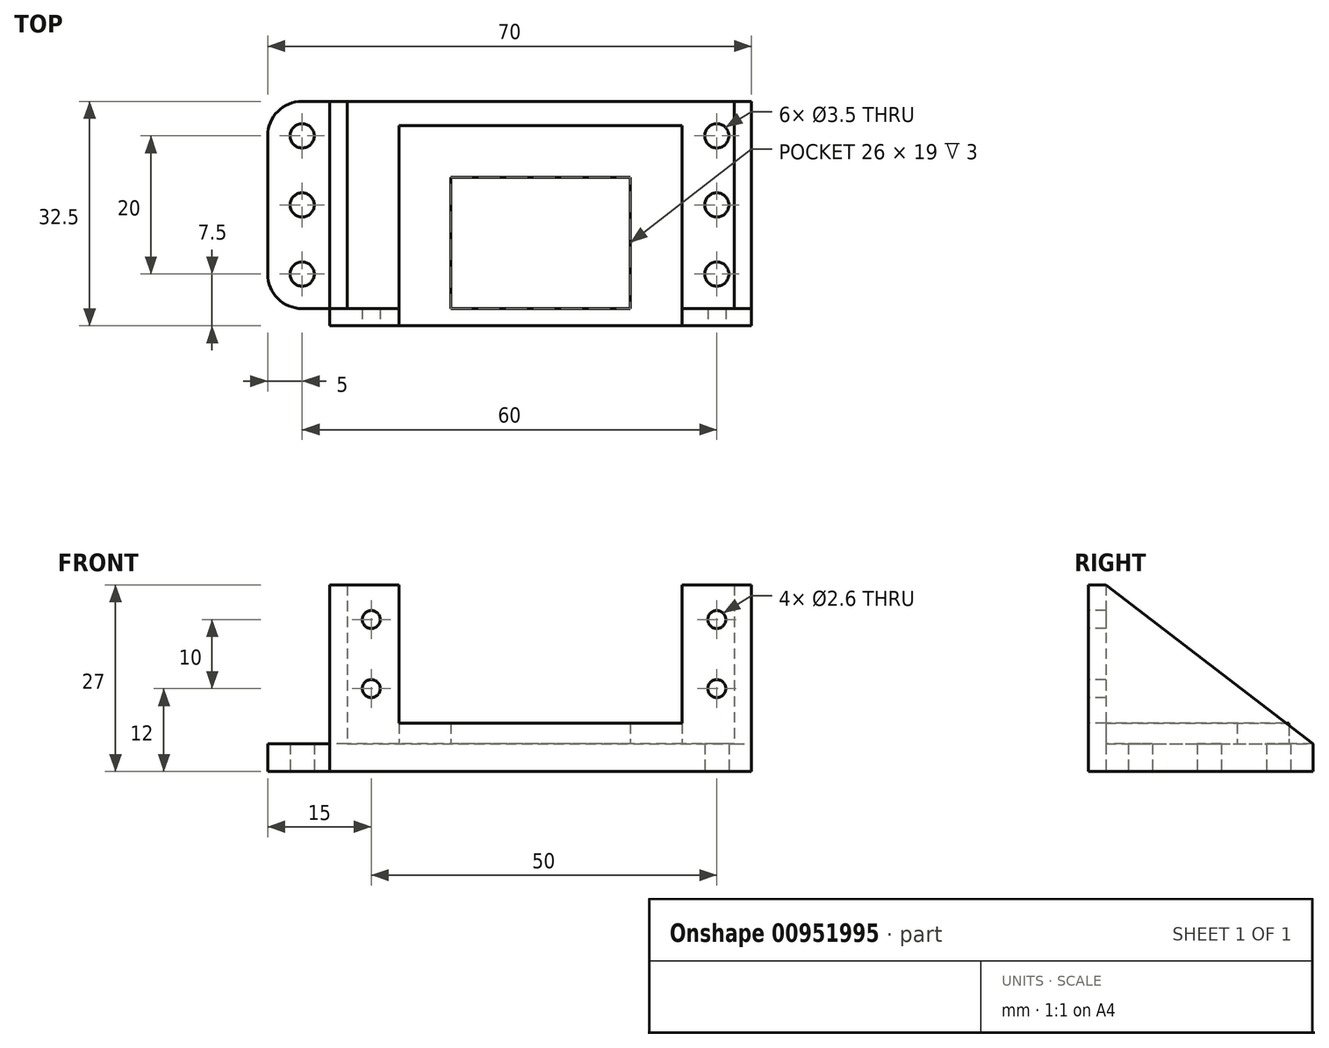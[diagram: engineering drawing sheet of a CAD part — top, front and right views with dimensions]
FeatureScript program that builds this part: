
annotation { "Feature Type Name" : "Feature", "Feature Type Description" : "" }
export const myFeature = defineFeature(function(context is Context, id is Id, definition is map)
    precondition{}
    {
        {
            var Q0;
            Q0=qCreatedBy(makeId("Top.planeOp"),FACE);
            var sketch = newSketch(context, id + "F0", { "sketchPlane" : qUnion([Q0])});
            skPoint(sketch, "E0", {"position": v(0, 0) * mm});
            skPoint(sketch, "E1.0.1.0", {"position": v(0, 10) * mm});
            skPoint(sketch, "E1.0.2.0", {"position": v(0, 20) * mm});
            skPoint(sketch, "E1.0.3.0", {"position": v(0, 30) * mm});
            skPoint(sketch, "E1.0.4.0", {"position": v(0, 40) * mm});
            skPoint(sketch, "E1.0.5.0", {"position": v(0, 50) * mm});
            skPoint(sketch, "E1.0.6.0", {"position": v(0, 60) * mm});
            skPoint(sketch, "E1.1.0.0", {"position": v(10, 0) * mm});
            skPoint(sketch, "E1.1.1.0", {"position": v(10, 10) * mm});
            skPoint(sketch, "E1.1.2.0", {"position": v(10, 20) * mm});
            skPoint(sketch, "E1.1.3.0", {"position": v(10, 30) * mm});
            skPoint(sketch, "E1.1.4.0", {"position": v(10, 40) * mm});
            skPoint(sketch, "E1.1.5.0", {"position": v(10, 50) * mm});
            skPoint(sketch, "E1.1.6.0", {"position": v(10, 60) * mm});
            skPoint(sketch, "E1.2.0.0", {"position": v(20, 0) * mm});
            skPoint(sketch, "E1.2.1.0", {"position": v(20, 10) * mm});
            skPoint(sketch, "E1.2.2.0", {"position": v(20, 20) * mm});
            skPoint(sketch, "E1.2.3.0", {"position": v(20, 30) * mm});
            skPoint(sketch, "E1.2.4.0", {"position": v(20, 40) * mm});
            skPoint(sketch, "E1.2.5.0", {"position": v(20, 50) * mm});
            skPoint(sketch, "E1.2.6.0", {"position": v(20, 60) * mm});
            skPoint(sketch, "E1.3.0.0", {"position": v(30, 0) * mm});
            skPoint(sketch, "E1.3.1.0", {"position": v(30, 10) * mm});
            skPoint(sketch, "E1.3.2.0", {"position": v(30, 20) * mm});
            skPoint(sketch, "E1.3.3.0", {"position": v(30, 30) * mm});
            skPoint(sketch, "E1.3.4.0", {"position": v(30, 40) * mm});
            skPoint(sketch, "E1.3.5.0", {"position": v(30, 50) * mm});
            skPoint(sketch, "E1.3.6.0", {"position": v(30, 60) * mm});
            skPoint(sketch, "E1.4.0.0", {"position": v(40, 0) * mm});
            skPoint(sketch, "E1.4.1.0", {"position": v(40, 10) * mm});
            skPoint(sketch, "E1.4.2.0", {"position": v(40, 20) * mm});
            skPoint(sketch, "E1.5.0.0", {"position": v(50, 0) * mm});
            skPoint(sketch, "E1.5.1.0", {"position": v(50, 10) * mm});
            skPoint(sketch, "E1.5.2.0", {"position": v(50, 20) * mm});
            skPoint(sketch, "E1.6.0.0", {"position": v(60, 0) * mm});
            skPoint(sketch, "E1.6.1.0", {"position": v(60, 10) * mm});
            skPoint(sketch, "E1.6.2.0", {"position": v(60, 20) * mm});
            skPoint(sketch, "E1.7.0.0", {"position": v(70, 0) * mm});
            skPoint(sketch, "E1.7.1.0", {"position": v(70, 10) * mm});
            skPoint(sketch, "E1.7.2.0", {"position": v(70, 20) * mm});
            skPoint(sketch, "E1.8.0.0", {"position": v(80, 0) * mm});
            skPoint(sketch, "E1.8.1.0", {"position": v(80, 10) * mm});
            skPoint(sketch, "E1.8.2.0", {"position": v(80, 20) * mm});
            skPoint(sketch, "E1.8.3.0", {"position": v(80, 30) * mm});
            skPoint(sketch, "E1.8.4.0", {"position": v(80, 40) * mm});
            skPoint(sketch, "E1.8.5.0", {"position": v(80, 50) * mm});
            skPoint(sketch, "E1.8.6.0", {"position": v(80, 60) * mm});
            skPoint(sketch, "E1.9.0.0", {"position": v(90, 0) * mm});
            skPoint(sketch, "E1.9.1.0", {"position": v(90, 10) * mm});
            skPoint(sketch, "E1.9.2.0", {"position": v(90, 20) * mm});
            skPoint(sketch, "E1.9.3.0", {"position": v(90, 30) * mm});
            skPoint(sketch, "E1.9.4.0", {"position": v(90, 40) * mm});
            skPoint(sketch, "E1.9.5.0", {"position": v(90, 50) * mm});
            skPoint(sketch, "E1.9.6.0", {"position": v(90, 60) * mm});
            skLineSegment(sketch, "E1.direction1", {"start": v(0, 0) * mm, "end": v(10, 0) * mm, "construction": true});
            skLineSegment(sketch, "E1.direction2", {"start": v(0, 0) * mm, "end": v(0, 10) * mm, "construction": true});
            skPoint(sketch, "E2.0.10.0", {"position": v(100, 0) * mm});
            skPoint(sketch, "E2.0.10.1", {"position": v(100, 10) * mm});
            skPoint(sketch, "E2.0.10.2", {"position": v(100, 20) * mm});
            skPoint(sketch, "E2.0.10.3", {"position": v(100, 30) * mm});
            skPoint(sketch, "E2.0.10.4", {"position": v(100, 40) * mm});
            skPoint(sketch, "E2.0.10.5", {"position": v(100, 50) * mm});
            skPoint(sketch, "E2.0.10.6", {"position": v(100, 60) * mm});
            skPoint(sketch, "E3.0.0.7", {"position": v(0, 70) * mm});
            skPoint(sketch, "E3.0.1.7", {"position": v(10, 70) * mm});
            skPoint(sketch, "E3.0.2.7", {"position": v(20, 70) * mm});
            skPoint(sketch, "E3.0.3.7", {"position": v(30, 70) * mm});
            skPoint(sketch, "E3.0.4.7", {"position": v(40, 70) * mm});
            skPoint(sketch, "E3.0.5.7", {"position": v(50, 70) * mm});
            skPoint(sketch, "E3.0.6.7", {"position": v(60, 70) * mm});
            skPoint(sketch, "E3.0.7.7", {"position": v(70, 70) * mm});
            skPoint(sketch, "E3.0.8.7", {"position": v(80, 70) * mm});
            skPoint(sketch, "E3.0.9.7", {"position": v(90, 70) * mm});
            skPoint(sketch, "E3.0.10.7", {"position": v(100, 70) * mm});
            skPoint(sketch, "E4.0.11.0", {"position": v(110, 0) * mm});
            skPoint(sketch, "E4.0.11.1", {"position": v(110, 10) * mm});
            skPoint(sketch, "E4.0.11.2", {"position": v(110, 20) * mm});
            skPoint(sketch, "E4.0.11.3", {"position": v(110, 30) * mm});
            skPoint(sketch, "E4.0.11.4", {"position": v(110, 40) * mm});
            skPoint(sketch, "E4.0.11.5", {"position": v(110, 50) * mm});
            skPoint(sketch, "E4.0.11.6", {"position": v(110, 60) * mm});
            skPoint(sketch, "E4.0.11.7", {"position": v(110, 70) * mm});
            skLineSegment(sketch, "E5", {"start": v(5, 24) * mm, "end": v(5, 11) * mm});
            skLineSegment(sketch, "E6", {"start": v(6, 10) * mm, "end": v(104, 10) * mm});
            skLineSegment(sketch, "E7", {"start": v(105, 11) * mm, "end": v(105, 24) * mm});
            skLineSegment(sketch, "E8", {"start": v(104, 25) * mm, "end": v(6, 25) * mm});
            skPoint(sketch, "E9.visualSharp", {"position": v(5, 25) * mm});
            skArc(sketch, "E9.filletArc", {"start": v(6, 25) * mm, "mid": v(5.3, 24.7) * mm, "end": v(5, 24) * mm});
            skPoint(sketch, "E10.visualSharp", {"position": v(5, 10) * mm});
            skArc(sketch, "E10.filletArc", {"start": v(5, 11) * mm, "mid": v(5.3, 10.3) * mm, "end": v(6, 10) * mm});
            skPoint(sketch, "E11.visualSharp", {"position": v(105, 25) * mm});
            skArc(sketch, "E11.filletArc", {"start": v(105, 24) * mm, "mid": v(104.7, 24.7) * mm, "end": v(104, 25) * mm});
            skPoint(sketch, "E12.visualSharp", {"position": v(105, 10) * mm});
            skArc(sketch, "E12.filletArc", {"start": v(104, 10) * mm, "mid": v(104.7, 10.3) * mm, "end": v(105, 11) * mm});
            skLineSegment(sketch, "E13", {"start": v(55, 10) * mm, "end": v(55, 76.51) * mm});
            skSolve(sketch);
        }
        {
            var Q0;
            Q0=qCreatedBy(makeId("Top.planeOp"),FACE);
            var sketch = newSketch(context, id + "F1", { "sketchPlane" : qUnion([Q0])});
            skLineSegment(sketch, "E14.0", {"start": v(104, 25) * mm, "end": v(6, 25) * mm});
            skLineSegment(sketch, "E15.bottom", {"start": v(36.5, 35) * mm, "end": v(92.5, 35) * mm});
            skLineSegment(sketch, "E15.top", {"start": v(36.5, 32.5) * mm, "end": v(92.5, 32.5) * mm});
            skLineSegment(sketch, "E15.left", {"start": v(36.5, 35) * mm, "end": v(36.5, 32.5) * mm});
            skLineSegment(sketch, "E15.right", {"start": v(92.5, 35) * mm, "end": v(92.5, 32.5) * mm});
            skLineSegment(sketch, "E16", {"start": v(44, 35) * mm, "end": v(44, 32.5) * mm});
            skLineSegment(sketch, "E17", {"start": v(85, 35) * mm, "end": v(85, 32.5) * mm});
            skLineSegment(sketch, "E18", {"start": v(36.5, 35) * mm, "end": v(25, 35) * mm});
            skLineSegment(sketch, "E19", {"start": v(25, 35) * mm, "end": v(25, 65) * mm});
            skLineSegment(sketch, "E20", {"start": v(25, 65) * mm, "end": v(36.5, 65) * mm});
            skLineSegment(sketch, "E21", {"start": v(36.5, 65) * mm, "end": v(95, 65) * mm});
            skLineSegment(sketch, "E22", {"start": v(95, 65) * mm, "end": v(95, 35) * mm});
            skLineSegment(sketch, "E23", {"start": v(95, 35) * mm, "end": v(92.5, 35) * mm});
            skLineSegment(sketch, "E24", {"start": v(36.5, 32.5) * mm, "end": v(34, 32.5) * mm});
            skLineSegment(sketch, "E25", {"start": v(34, 32.5) * mm, "end": v(34, 35) * mm});
            skLineSegment(sketch, "E26", {"start": v(92.5, 32.5) * mm, "end": v(95, 32.5) * mm});
            skLineSegment(sketch, "E27", {"start": v(95, 32.5) * mm, "end": v(95, 35) * mm});
            skLineSegment(sketch, "E28", {"start": v(44, 35) * mm, "end": v(44, 61.5) * mm});
            skLineSegment(sketch, "E29", {"start": v(44, 61.5) * mm, "end": v(85, 61.5) * mm});
            skLineSegment(sketch, "E30", {"start": v(85, 61.5) * mm, "end": v(85, 35) * mm});
            skLineSegment(sketch, "E31", {"start": v(51.5, 35) * mm, "end": v(51.5, 54) * mm});
            skLineSegment(sketch, "E32", {"start": v(51.5, 54) * mm, "end": v(77.5, 54) * mm});
            skLineSegment(sketch, "E33", {"start": v(77.5, 54) * mm, "end": v(77.5, 35) * mm});
            skCircle(sketch, "E34", {"center": v(30, 40) * mm, "radius": 1.75 * mm});
            skCircle(sketch, "E35", {"center": v(30, 50) * mm, "radius": 1.75 * mm});
            skCircle(sketch, "E36", {"center": v(30, 60) * mm, "radius": 1.75 * mm});
            skCircle(sketch, "E37", {"center": v(90, 40) * mm, "radius": 1.75 * mm});
            skCircle(sketch, "E38", {"center": v(90, 50) * mm, "radius": 1.75 * mm});
            skCircle(sketch, "E39", {"center": v(90, 60) * mm, "radius": 1.75 * mm});
            skSolve(sketch);
        }
        {
            var Q0;
            {var subQ1=sQuery(id+"F1.wireOp",EDGE,"E19");Q0=makeQuery(id+"F1.imprint","IMPRINT",FACE,{"disambiguationData":[TD([[makeQuery(id+"F1.imprint","IMPRINT",EDGE,{"derivedFrom":subQ1}),-1.0]])]});}
            var Q1;
            {var subQ0=sQuery(id+"F1.wireOp",EDGE,"E28");Q1=makeQuery(id+"F1.imprint","IMPRINT",FACE,{"disambiguationData":[TD([[makeQuery(id+"F1.imprint","IMPRINT",EDGE,{"derivedFrom":subQ0}),-1.0]])]});}
            var Q2;
            {var subQ0=sQuery(id+"F1.wireOp",EDGE,"E31");Q2=makeQuery(id+"F1.imprint","IMPRINT",FACE,{"disambiguationData":[TD([[makeQuery(id+"F1.imprint","IMPRINT",EDGE,{"derivedFrom":subQ0}),-1.0]])]});}
            var Q3;
            {var subQ0=sQuery(id+"F1.wireOp",EDGE,"E15.left");Q3=makeQuery(id+"F1.imprint","IMPRINT",FACE,{"disambiguationData":[TD([[makeQuery(id+"F1.imprint","IMPRINT",EDGE,{"derivedFrom":subQ0}),-1.0]])]});}
            var Q4;
            {var subQ0=sQuery(id+"F1.wireOp",EDGE,"E15.left");Q4=makeQuery(id+"F1.imprint","IMPRINT",FACE,{"disambiguationData":[TD([[makeQuery(id+"F1.imprint","IMPRINT",EDGE,{"derivedFrom":subQ0}),1.0]])]});}
            var Q5;
            {var subQ4=sQuery(id+"F1.wireOp",EDGE,"E16");Q5=makeQuery(id+"F1.imprint","IMPRINT",FACE,{"disambiguationData":[TD([[makeQuery(id+"F1.imprint","IMPRINT",EDGE,{"derivedFrom":subQ4}),1.0]])]});}
            var Q6;
            {var subQ0=sQuery(id+"F1.wireOp",EDGE,"E15.right");Q6=makeQuery(id+"F1.imprint","IMPRINT",FACE,{"disambiguationData":[TD([[makeQuery(id+"F1.imprint","IMPRINT",EDGE,{"derivedFrom":subQ0}),-1.0]])]});}
            var Q7;
            Q7=makeQuery(id+"F1.imprint","IMPRINT",FACE,{"disambiguationData":[TD([[makeQuery(id+"F1.imprint","IMPRINT",EDGE,{"derivedFrom":sQuery(id+"F1.wireOp",EDGE,"E15.right")}),1.0]])]});
            extrude(context, id + "F2", {"entities" : qUnion([Q0, Q1, Q2, Q3, Q4, Q5, Q6, Q7]), "depth" : 4 * mm, "offsetDistance" : 25 * mm});
        }
        {
            var Q0;
            {var subQ0=sQuery(id+"F1.wireOp",EDGE,"E28");Q0=makeQuery(id+"F1.imprint","IMPRINT",FACE,{"disambiguationData":[TD([[makeQuery(id+"F1.imprint","IMPRINT",EDGE,{"derivedFrom":subQ0}),-1.0]])]});}
            var Q1;
            {var subQ4=sQuery(id+"F1.wireOp",EDGE,"E16");Q1=makeQuery(id+"F1.imprint","IMPRINT",FACE,{"disambiguationData":[TD([[makeQuery(id+"F1.imprint","IMPRINT",EDGE,{"derivedFrom":subQ4}),1.0]])]});}
            extrude(context, id + "F3", {"entities" : qUnion([Q0, Q1]), "operationType" : NewBodyOperationType.ADD, "depth" : (4 + 3) * mm, "offsetDistance" : 25 * mm});
        }
        {
            var Q0;
            {var subQ0=sQuery(id+"F1.wireOp",EDGE,"E15.left");Q0=makeQuery(id+"F1.imprint","IMPRINT",FACE,{"disambiguationData":[TD([[makeQuery(id+"F1.imprint","IMPRINT",EDGE,{"derivedFrom":subQ0}),1.0]])]});}
            var Q1;
            {var subQ0=sQuery(id+"F1.wireOp",EDGE,"E15.right");Q1=makeQuery(id+"F1.imprint","IMPRINT",FACE,{"disambiguationData":[TD([[makeQuery(id+"F1.imprint","IMPRINT",EDGE,{"derivedFrom":subQ0}),-1.0]])]});}
            var Q2;
            Q2=makeQuery(id+"F1.imprint","IMPRINT",FACE,{"disambiguationData":[TD([[makeQuery(id+"F1.imprint","IMPRINT",EDGE,{"derivedFrom":sQuery(id+"F1.wireOp",EDGE,"E15.right")}),1.0]])]});
            var Q3;
            {var subQ0=sQuery(id+"F1.wireOp",EDGE,"E15.left");Q3=makeQuery(id+"F1.imprint","IMPRINT",FACE,{"disambiguationData":[TD([[makeQuery(id+"F1.imprint","IMPRINT",EDGE,{"derivedFrom":subQ0}),-1.0]])]});}
            extrude(context, id + "F4", {"entities" : qUnion([Q0, Q1, Q2, Q3]), "operationType" : NewBodyOperationType.ADD, "depth" : 27 * mm, "offsetDistance" : 25 * mm});
        }
        {
            var Q0;
            {var subQ0=sQuery(id+"F1.wireOp",EDGE,"E27");Q0=makeQuery(id+"F4.boolean.opBoolean","MERGE",FACE,{"derivedFrom":[makeQuery(id+"F2.opExtrude","SWEPT_FACE",FACE,{"disambiguationData":[OSD([sQuery(id+"F1.wireOp",EDGE,"E22"),subQ0])]}),makeQuery(id+"F4.opExtrude","SWEPT_FACE",FACE,{"disambiguationData":[OSD([subQ0])]})]});}
            var sketch = newSketch(context, id + "F5", { "sketchPlane" : qUnion([Q0])});
            skLineSegment(sketch, "E40", {"start": v(35, 27) * mm, "end": v(65, 4) * mm});
            skSolve(sketch);
        }
        {
            var Q0;
            Q0=makeQuery(id+"F5.imprint","IMPRINT",FACE,{"disambiguationData":[TD([[makeQuery(id+"F5.imprint","IMPRINT",EDGE,{"derivedFrom":sQuery(id+"F5.wireOp",EDGE,"E40")}),-1.0]])]});
            extrude(context, id + "F6", {"entities" : qUnion([Q0]), "operationType" : NewBodyOperationType.ADD, "oppositeDirection" : true, "depth" : 2.5 * mm, "offsetDistance" : 25 * mm});
        }
        {
            var Q0;
            {var subQ0=sQuery(id+"F1.wireOp",EDGE,"E25");Q0=makeQuery(id+"F4.boolean.opBoolean","MERGE",FACE,{"derivedFrom":[makeQuery(id+"F2.opExtrude","SWEPT_FACE",FACE,{"disambiguationData":[OSD([subQ0])]}),makeQuery(id+"F4.opExtrude","SWEPT_FACE",FACE,{"disambiguationData":[OSD([subQ0])]})]});}
            var sketch = newSketch(context, id + "F7", { "sketchPlane" : qUnion([Q0])});
            skLineSegment(sketch, "E41.0", {"start": v(-35, 4) * mm, "end": v(-65, 4) * mm});
            skLineSegment(sketch, "E42", {"start": v(-65, 4) * mm, "end": v(-35, 27) * mm});
            skLineSegment(sketch, "E43", {"start": v(-35, 27) * mm, "end": v(-35, 4) * mm});
            skSolve(sketch);
        }
        {
            var Q0;
            Q0=makeQuery(id+"F7.imprint","IMPRINT",FACE,{"disambiguationData":[TD([[makeQuery(id+"F7.imprint","IMPRINT",EDGE,{"derivedFrom":sQuery(id+"F7.wireOp",EDGE,"E41.0")}),-1.0]])]});
            extrude(context, id + "F8", {"entities" : qUnion([Q0]), "operationType" : NewBodyOperationType.ADD, "oppositeDirection" : true, "depth" : 2.5 * mm, "offsetDistance" : 25 * mm});
        }
        {
            var Q0;
            Q0=makeQuery(id+"F2.opExtrude","SWEPT_EDGE",EDGE,{"disambiguationData":[OSD([sQuery(id+"F1.wireOp",EDGE,"E18"),sQuery(id+"F1.wireOp",EDGE,"E19")])]});
            var Q1;
            Q1=makeQuery(id+"F2.opExtrude","SWEPT_EDGE",EDGE,{"disambiguationData":[OSD([sQuery(id+"F1.wireOp",EDGE,"E19"),sQuery(id+"F1.wireOp",EDGE,"E20")])]});
            fillet(context, id + "F9", {"entities" : qUnion([Q0, Q1]), "radius" : 5 * mm, "tangentPropagation" : true, "allowEdgeOverflow" : false});
        }
        {
            var Q0;
            {var subQ0=sQuery(id+"F1.wireOp",EDGE,"E26");var subQ1=sQuery(id+"F1.wireOp",EDGE,"E15.top");var subQ2=sQuery(id+"F1.wireOp",EDGE,"E24");Q0=makeQuery(id+"F4.boolean.opBoolean","MERGE",FACE,{"derivedFrom":[makeQuery(id+"F3.boolean.opBoolean","MERGE",FACE,{"derivedFrom":[makeQuery(id+"F2.opExtrude","SWEPT_FACE",FACE,{"disambiguationData":[OSD([subQ1,subQ2,subQ0])]}),makeQuery(id+"F3.opExtrude","SWEPT_FACE",FACE,{"disambiguationData":[OSD([subQ1])]})]}),makeQuery(id+"F4.opExtrude","SWEPT_FACE",FACE,{"disambiguationData":[OSD([subQ1,subQ2])]}),makeQuery(id+"F4.opExtrude","SWEPT_FACE",FACE,{"disambiguationData":[OSD([subQ1,subQ0])]})]});}
            var sketch = newSketch(context, id + "F10", { "sketchPlane" : qUnion([Q0])});
            skCircle(sketch, "E44", {"center": v(40, 22) * mm, "radius": 1.3 * mm});
            skCircle(sketch, "E45", {"center": v(40, 12) * mm, "radius": 1.3 * mm});
            skCircle(sketch, "E46", {"center": v(90, 12) * mm, "radius": 1.3 * mm});
            skCircle(sketch, "E47", {"center": v(90, 22) * mm, "radius": 1.3 * mm});
            skSolve(sketch);
        }
        {
            var Q0;
            Q0=makeQuery(id+"F10.imprint","IMPRINT",FACE,{"disambiguationData":[TD([[makeQuery(id+"F10.imprint","IMPRINT",EDGE,{"derivedFrom":sQuery(id+"F10.wireOp",EDGE,"E44")}),1.0]])]});
            var Q1;
            Q1=makeQuery(id+"F10.imprint","IMPRINT",FACE,{"disambiguationData":[TD([[makeQuery(id+"F10.imprint","IMPRINT",EDGE,{"derivedFrom":sQuery(id+"F10.wireOp",EDGE,"E45")}),1.0]])]});
            var Q2;
            Q2=makeQuery(id+"F10.imprint","IMPRINT",FACE,{"disambiguationData":[TD([[makeQuery(id+"F10.imprint","IMPRINT",EDGE,{"derivedFrom":sQuery(id+"F10.wireOp",EDGE,"E46")}),1.0]])]});
            var Q3;
            Q3=makeQuery(id+"F10.imprint","IMPRINT",FACE,{"disambiguationData":[TD([[makeQuery(id+"F10.imprint","IMPRINT",EDGE,{"derivedFrom":sQuery(id+"F10.wireOp",EDGE,"E47")}),1.0]])]});
            extrude(context, id + "F11", {"entities" : qUnion([Q0, Q1, Q2, Q3]), "operationType" : NewBodyOperationType.REMOVE, "oppositeDirection" : true, "depth" : 25 * mm, "offsetDistance" : 25 * mm});
        }
    });
